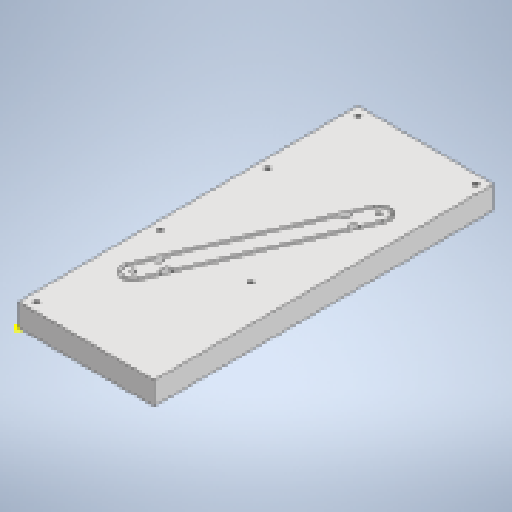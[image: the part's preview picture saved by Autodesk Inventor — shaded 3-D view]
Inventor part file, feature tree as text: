
AUTODESK INVENTOR PART (.ipt)
format: ipt  version: 2023 (Build 270158000, 158)  size: 225,792 bytes
history: native  units: mm
features: reference x9, thread x6, sketch x4, extrude x3, other x3
ambient origin geometry x8: Origin, YZ Plane, XZ Plane, XY Plane, X Axis, Y Axis, Z Axis, Center Point
bodies: Solid1 (feature_tree)
feature tree (25):
  extrude  "Extrusion1"  Depth=60.0mm
  sketch  "Sketch2"  dims[d2=10.0mm d3=0.0mm d4=2.2mm d5=2.2mm d6=2.2mm d7=2.2mm d8=2.2mm d9=2.2mm d10=10.0mm d11=0.0mm]
  extrude  "Extrusion2"  Depth=10.0mm
  thread  "Thread1"  [1 undecoded]
  thread  "Thread2"  [1 undecoded]
  thread  "Thread3"  [1 undecoded]
  thread  "Thread4"  [1 undecoded]
  thread  "Thread5"  [1 undecoded]
  thread  "Thread6"  [1 undecoded]
  extrude  "Extrusion3"  Depth=10.0mm TaperAngle=0.0deg
  sketch  "Sketch1"  dims[d0=150.0mm d1=60.0mm]
  reference  "Reference1"
  reference  "Reference2"
  reference  "Reference3"
  reference  "Reference4"
  reference  "Reference5"
  reference  "Reference6"
  sketch  "Sketch3"  dims[d12=10.0mm d13=0.0mm d14=10.0mm d15=0.0mm]
  sketch  "Sketch4"  dims[d16=10.0mm d17=0.0mm d18=10.0mm d19=0.0mm d20=10.0mm d21=0.0mm d22=10.0mm d23=0.0mm d24=10.0mm d25=22.5mm d26=35.0mm d27=35.0mm d28=7.0mm d29=7.0mm d30=4.0mm d31=4.0mm d32=90.0deg d33=4.0mm d34=4.0mm d35=10.0mm d36=10.0mm d37=10.0mm d38=0.0mm d39=2.2mm d40=2.2mm]
  reference  "Reference7"
  reference  "Reference8"
  reference  "Reference9"
  other  "<userpath>\OneDrive\ClawdDrive\Objet3D\IminaProbe\V2\FlexK7V2.iam"
  other  "FlexK7V2.iam"
  other  "FlexK7V2:1"
note: 6 required parameter values undecoded (feature->parameter linkage not recoverable at this tier; creation-order binding heuristic only, values carry confidence <= 0.55)
